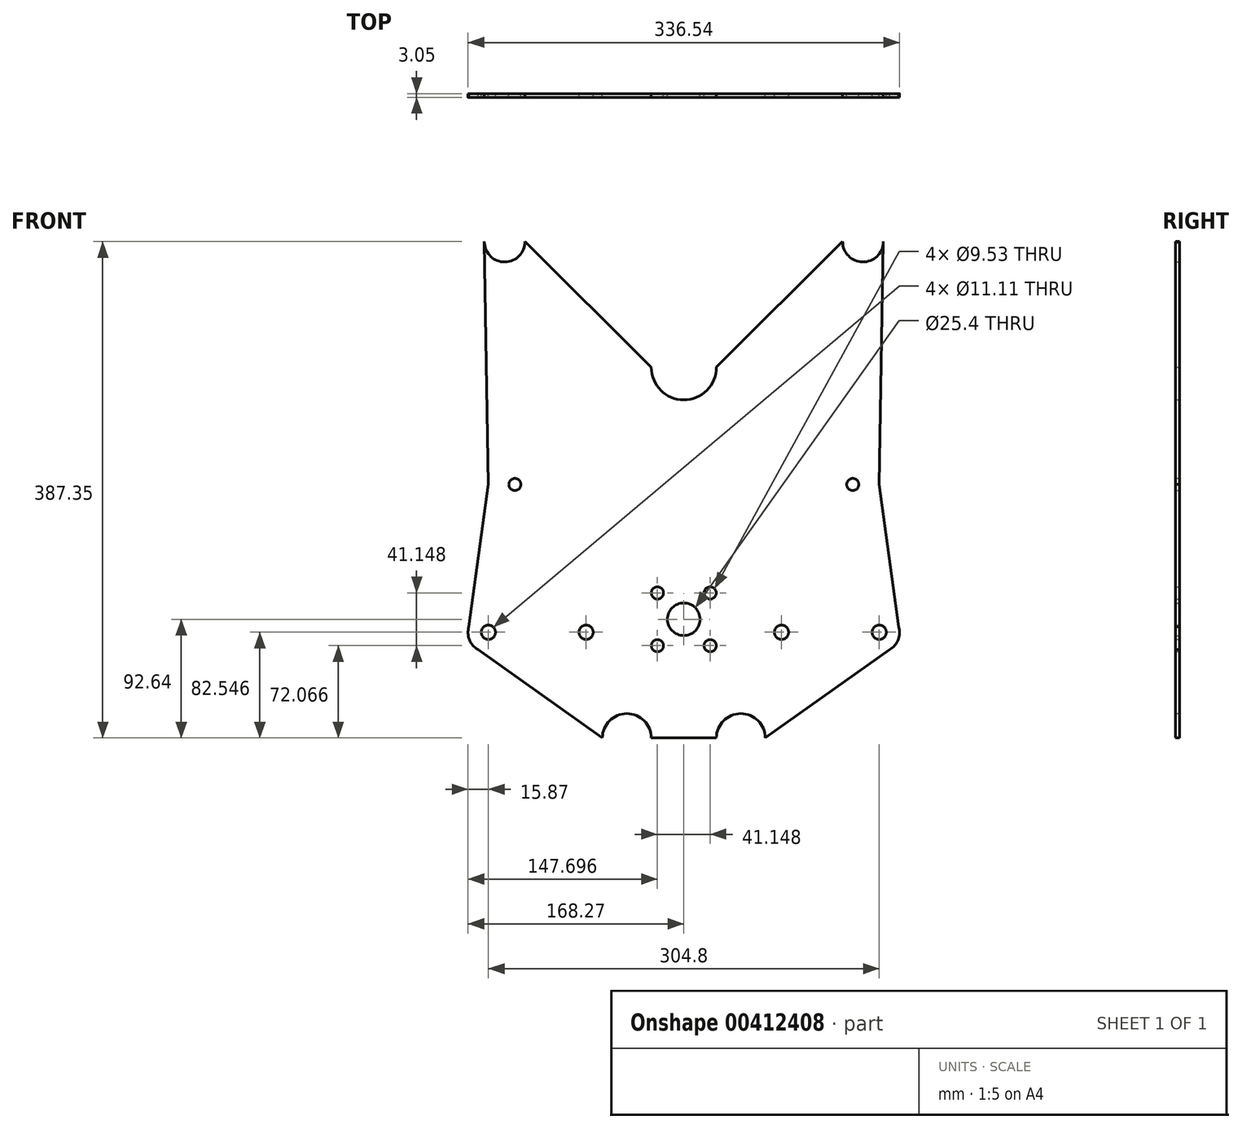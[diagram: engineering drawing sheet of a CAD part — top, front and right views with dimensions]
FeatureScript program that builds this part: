
annotation { "Feature Type Name" : "Feature", "Feature Type Description" : "" }
export const myFeature = defineFeature(function(context is Context, id is Id, definition is map)
    precondition{}
    {
        {
            var Q0;
            Q0=qCreatedBy(makeId("Front.planeOp"),FACE);
            var sketch = newSketch(context, id + "F0", { "sketchPlane" : qUnion([Q0])});
            skCircle(sketch, "E0", {"center": v(0, 0) * mm, "radius": 12.7 * mm});
            skLineSegment(sketch, "E1.bottom", {"start": v(20.57, -20.57) * mm, "end": v(-20.57, -20.57) * mm, "construction": true});
            skLineSegment(sketch, "E1.top", {"start": v(20.57, 20.57) * mm, "end": v(-20.57, 20.57) * mm, "construction": true});
            skLineSegment(sketch, "E1.left", {"start": v(20.57, -20.57) * mm, "end": v(20.57, 20.57) * mm, "construction": true});
            skLineSegment(sketch, "E1.right", {"start": v(-20.57, -20.57) * mm, "end": v(-20.57, 20.57) * mm, "construction": true});
            skCircle(sketch, "E2", {"center": v(-20.57, 20.57) * mm, "radius": 4.76 * mm});
            skCircle(sketch, "E3", {"center": v(20.57, 20.57) * mm, "radius": 4.76 * mm});
            skCircle(sketch, "E4", {"center": v(20.57, -20.57) * mm, "radius": 4.76 * mm});
            skCircle(sketch, "E5", {"center": v(-20.57, -20.57) * mm, "radius": 4.76 * mm});
            skPoint(sketch, "E6", {"position": v(20.57, -15.81) * mm});
            skPoint(sketch, "E7", {"position": v(-20.57, -15.81) * mm});
            skLineSegment(sketch, "E8", {"start": v(0, -15.81) * mm, "end": v(152.4, -15.81) * mm, "construction": true});
            skPoint(sketch, "E8.startSnap0", {"position": v(0, -20.57) * mm});
            skLineSegment(sketch, "E9", {"start": v(0, -15.81) * mm, "end": v(-152.4, -15.81) * mm, "construction": true});
            skCircle(sketch, "E10", {"center": v(-152.4, -10.1) * mm, "radius": 5.56 * mm});
            skCircle(sketch, "E11", {"center": v(152.4, -10.1) * mm, "radius": 5.56 * mm});
            skCircle(sketch, "E12", {"center": v(76.2, -10.1) * mm, "radius": 5.56 * mm});
            skCircle(sketch, "E13", {"center": v(-76.2, -10.1) * mm, "radius": 5.56 * mm});
            skPoint(sketch, "E14", {"position": v(-152.4, 105.22) * mm});
            skLineSegment(sketch, "E15", {"start": v(0, 0) * mm, "end": v(0, 140.85) * mm, "construction": true});
            skPoint(sketch, "E15.endSnap0", {"position": v(0, 20.57) * mm});
            skLineSegment(sketch, "E16", {"start": v(-152.4, -10.1) * mm, "end": v(-152.4, -92.64) * mm, "construction": true});
            skLineSegment(sketch, "E17", {"start": v(-152.4, -10.1) * mm, "end": v(-152.4, 294.7) * mm, "construction": true});
            skLineSegment(sketch, "E18", {"start": v(-152.4, 105.22) * mm, "end": v(152.4, 105.22) * mm, "construction": true});
            skCircle(sketch, "E19", {"center": v(-131.75, 105.22) * mm, "radius": 4.72 * mm});
            skCircle(sketch, "E20", {"center": v(131.75, 105.22) * mm, "radius": 4.7 * mm});
            skLineSegment(sketch, "E21", {"start": v(-152.4, -92.64) * mm, "end": v(152.4, -92.64) * mm, "construction": true});
            skPoint(sketch, "E22", {"position": v(-44.45, -92.64) * mm});
            skLineSegment(sketch, "E23", {"start": v(0, -20.57) * mm, "end": v(0, -115.22) * mm, "construction": true});
            skPoint(sketch, "E24", {"position": v(44.45, -92.64) * mm});
            skArc(sketch, "E25", {"start": v(-25.4, -92.64) * mm, "mid": v(-44.45, -73.6) * mm, "end": v(-63.5, -92.64) * mm});
            skArc(sketch, "E26", {"start": v(63.5, -92.64) * mm, "mid": v(44.45, -73.6) * mm, "end": v(25.4, -92.64) * mm});
            skLineSegment(sketch, "E27", {"start": v(-25.4, -92.64) * mm, "end": v(25.4, -92.64) * mm});
            skLineSegment(sketch, "E28", {"start": v(0, 0) * mm, "end": v(0, 293.77) * mm, "construction": true});
            skLineSegment(sketch, "E29", {"start": v(152.4, 294.7) * mm, "end": v(-152.4, 294.7) * mm, "construction": true});
            skPoint(sketch, "E30", {"position": v(-139.7, 294.7) * mm});
            skPoint(sketch, "E31", {"position": v(139.7, 294.7) * mm});
            skArc(sketch, "E32", {"start": v(-155.58, 294.7) * mm, "mid": v(-139.7, 278.83) * mm, "end": v(-123.83, 294.7) * mm});
            skArc(sketch, "E33", {"start": v(123.83, 294.7) * mm, "mid": v(139.7, 278.83) * mm, "end": v(155.58, 294.7) * mm});
            skArc(sketch, "E34", {"start": v(-25.4, 196.65) * mm, "mid": v(0, 171.26) * mm, "end": v(25.4, 196.65) * mm});
            skLineSegment(sketch, "E35", {"start": v(-123.83, 294.7) * mm, "end": v(-25.4, 196.65) * mm});
            skLineSegment(sketch, "E36", {"start": v(123.83, 294.7) * mm, "end": v(25.4, 196.65) * mm});
            skArc(sketch, "E37", {"start": v(160.54, -23.72) * mm, "mid": v(167.15, -15.97) * mm, "end": v(167.68, -5.8) * mm});
            skArc(sketch, "E38", {"start": v(-167.68, -5.8) * mm, "mid": v(-167.15, -15.97) * mm, "end": v(-160.54, -23.72) * mm});
            skLineSegment(sketch, "E39", {"start": v(155.58, 294.7) * mm, "end": v(155.57, 294.17) * mm});
            skLineSegment(sketch, "E40", {"start": v(152.4, 105.22) * mm, "end": v(168.28, -10.1) * mm});
            skLineSegment(sketch, "E41", {"start": v(-155.58, 294.7) * mm, "end": v(-152.4, 105.22) * mm});
            skLineSegment(sketch, "E42", {"start": v(-152.4, 105.22) * mm, "end": v(-168.28, -10.1) * mm});
            skLineSegment(sketch, "E43", {"start": v(155.58, 294.7) * mm, "end": v(152.4, 105.22) * mm});
            skLineSegment(sketch, "E44", {"start": v(162.59, -22.27) * mm, "end": v(63.5, -92.64) * mm});
            skLineSegment(sketch, "E45", {"start": v(-162.59, -22.27) * mm, "end": v(-63.5, -92.64) * mm});
            skSolve(sketch);
        }
        {
            var Q0;
            Q0 = qSketchRegion(id + "F0", true);
            extrude(context, id + "F1", {"entities" : qUnion([Q0]), "depth" : 3.05 * mm});
        }
    });
